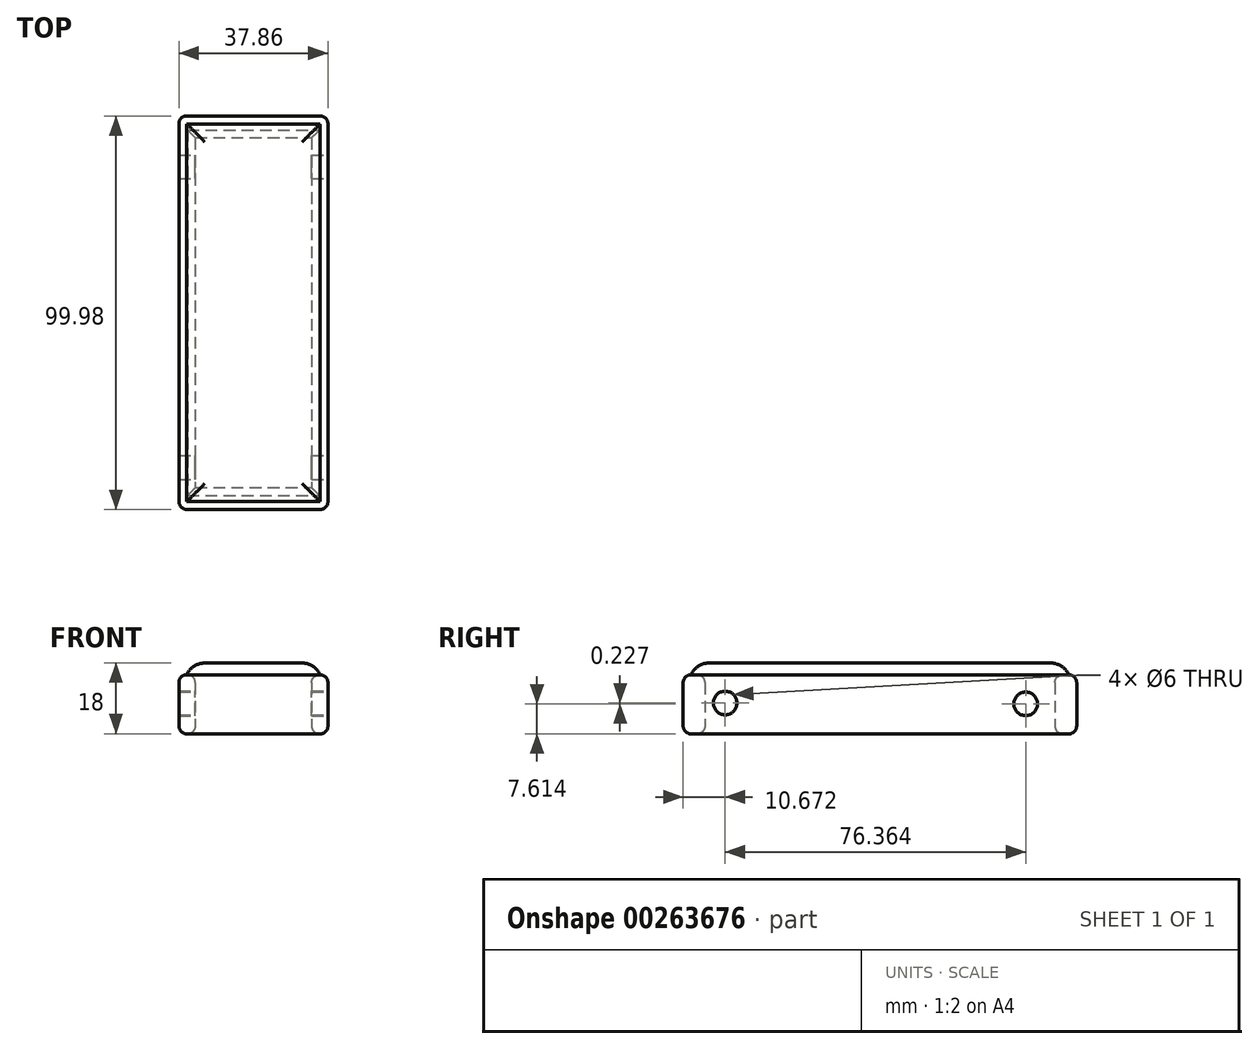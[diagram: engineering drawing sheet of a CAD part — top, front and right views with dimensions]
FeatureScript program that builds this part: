
annotation { "Feature Type Name" : "Feature", "Feature Type Description" : "" }
export const myFeature = defineFeature(function(context is Context, id is Id, definition is map)
    precondition{}
    {
        {
            var Q0;
            Q0=qCreatedBy(makeId("Top.planeOp"),FACE);
            var sketch = newSketch(context, id + "F0", { "sketchPlane" : qUnion([Q0])});
            skLineSegment(sketch, "E0.bottom", {"start": v(-18.93, 50) * mm, "end": v(18.93, 50) * mm});
            skLineSegment(sketch, "E0.top", {"start": v(-18.93, -50) * mm, "end": v(18.93, -50) * mm});
            skLineSegment(sketch, "E0.left", {"start": v(-18.93, 50) * mm, "end": v(-18.93, -50) * mm});
            skLineSegment(sketch, "E0.right", {"start": v(18.93, 50) * mm, "end": v(18.93, -50) * mm});
            skPoint(sketch, "E0.middle", {"position": v(0, 0) * mm});
            skLineSegment(sketch, "E1.bottom", {"start": v(-14.78, 44.45) * mm, "end": v(14.78, 44.45) * mm});
            skLineSegment(sketch, "E1.top", {"start": v(-14.78, -44.45) * mm, "end": v(14.78, -44.45) * mm});
            skLineSegment(sketch, "E1.left", {"start": v(-14.78, 44.45) * mm, "end": v(-14.78, -44.45) * mm});
            skLineSegment(sketch, "E1.right", {"start": v(14.78, 44.45) * mm, "end": v(14.78, -44.45) * mm});
            skSolve(sketch);
        }
        {
            var Q0;
            Q0 = qSketchRegion(id + "F0", true);
            extrude(context, id + "F1", {"entities" : qUnion([Q0]), "depth" : 15 * mm});
        }
        {
            var Q0;
            Q0=makeQuery(id+"F1.opExtrude","CAP_EDGE",EDGE,{"disambiguationData":[OSD([sQuery(id+"F0.wireOp",EDGE,"E0.bottom")])],"isStart":false});
            var Q1;
            Q1=makeQuery(id+"F1.opExtrude","CAP_EDGE",EDGE,{"disambiguationData":[OSD([sQuery(id+"F0.wireOp",EDGE,"E0.left")])],"isStart":false});
            var Q2;
            Q2=makeQuery(id+"F1.opExtrude","CAP_EDGE",EDGE,{"disambiguationData":[OSD([sQuery(id+"F0.wireOp",EDGE,"E0.top")])],"isStart":false});
            var Q3;
            Q3=makeQuery(id+"F1.opExtrude","CAP_EDGE",EDGE,{"disambiguationData":[OSD([sQuery(id+"F0.wireOp",EDGE,"E0.right")])],"isStart":false});
            var Q4;
            Q4=makeQuery(id+"F1.opExtrude","SWEPT_EDGE",EDGE,{"disambiguationData":[OSD([sQuery(id+"F0.wireOp",EDGE,"E0.bottom"),sQuery(id+"F0.wireOp",EDGE,"E0.left")])]});
            var Q5;
            Q5=makeQuery(id+"F1.opExtrude","SWEPT_EDGE",EDGE,{"disambiguationData":[OSD([sQuery(id+"F0.wireOp",EDGE,"E0.top"),sQuery(id+"F0.wireOp",EDGE,"E0.left")])]});
            var Q6;
            Q6=makeQuery(id+"F1.opExtrude","SWEPT_EDGE",EDGE,{"disambiguationData":[OSD([sQuery(id+"F0.wireOp",EDGE,"E0.bottom"),sQuery(id+"F0.wireOp",EDGE,"E0.right")])]});
            var Q7;
            Q7=makeQuery(id+"F1.opExtrude","SWEPT_EDGE",EDGE,{"disambiguationData":[OSD([sQuery(id+"F0.wireOp",EDGE,"E0.top"),sQuery(id+"F0.wireOp",EDGE,"E0.right")])]});
            var Q8;
            Q8=makeQuery(id+"F1.opExtrude","CAP_EDGE",EDGE,{"disambiguationData":[OSD([sQuery(id+"F0.wireOp",EDGE,"E1.right")])],"isStart":false});
            var Q9;
            Q9=makeQuery(id+"F1.opExtrude","CAP_EDGE",EDGE,{"disambiguationData":[OSD([sQuery(id+"F0.wireOp",EDGE,"E1.left")])],"isStart":false});
            var Q10;
            Q10=makeQuery(id+"F1.opExtrude","CAP_EDGE",EDGE,{"disambiguationData":[OSD([sQuery(id+"F0.wireOp",EDGE,"E1.top")])],"isStart":false});
            var Q11;
            Q11=makeQuery(id+"F1.opExtrude","CAP_EDGE",EDGE,{"disambiguationData":[OSD([sQuery(id+"F0.wireOp",EDGE,"E1.bottom")])],"isStart":false});
            var Q12;
            Q12=makeQuery(id+"F1.opExtrude","CAP_EDGE",EDGE,{"disambiguationData":[OSD([sQuery(id+"F0.wireOp",EDGE,"E1.top")])],"isStart":true});
            var Q13;
            Q13=makeQuery(id+"F1.opExtrude","CAP_EDGE",EDGE,{"disambiguationData":[OSD([sQuery(id+"F0.wireOp",EDGE,"E0.top")])],"isStart":true});
            var Q14;
            Q14=makeQuery(id+"F1.opExtrude","CAP_EDGE",EDGE,{"disambiguationData":[OSD([sQuery(id+"F0.wireOp",EDGE,"E1.left")])],"isStart":true});
            var Q15;
            Q15=makeQuery(id+"F1.opExtrude","CAP_EDGE",EDGE,{"disambiguationData":[OSD([sQuery(id+"F0.wireOp",EDGE,"E0.right")])],"isStart":true});
            var Q16;
            Q16=makeQuery(id+"F1.opExtrude","CAP_EDGE",EDGE,{"disambiguationData":[OSD([sQuery(id+"F0.wireOp",EDGE,"E1.right")])],"isStart":true});
            var Q17;
            Q17=makeQuery(id+"F1.opExtrude","CAP_EDGE",EDGE,{"disambiguationData":[OSD([sQuery(id+"F0.wireOp",EDGE,"E1.bottom")])],"isStart":true});
            var Q18;
            Q18=makeQuery(id+"F1.opExtrude","CAP_EDGE",EDGE,{"disambiguationData":[OSD([sQuery(id+"F0.wireOp",EDGE,"E0.bottom")])],"isStart":true});
            var Q19;
            Q19=makeQuery(id+"F1.opExtrude","CAP_EDGE",EDGE,{"disambiguationData":[OSD([sQuery(id+"F0.wireOp",EDGE,"E0.left")])],"isStart":true});
            fillet(context, id + "F2", {"entities" : qUnion([Q0, Q1, Q2, Q3, Q4, Q5, Q6, Q7, Q8, Q9, Q10, Q11, Q12, Q13, Q14, Q15, Q16, Q17, Q18, Q19]), "radius" : 2 * mm, "tangentPropagation" : true, "allowEdgeOverflow" : false});
        }
        {
            var Q0;
            Q0=makeQuery(id+"F1.opExtrude","CAP_FACE",FACE,{"disambiguationData":[OSD([sQuery(id+"F0.wireOp",EDGE,"E0.bottom"),sQuery(id+"F0.wireOp",EDGE,"E0.top"),sQuery(id+"F0.wireOp",EDGE,"E0.left"),sQuery(id+"F0.wireOp",EDGE,"E0.right"),sQuery(id+"F0.wireOp",EDGE,"E1.bottom"),sQuery(id+"F0.wireOp",EDGE,"E1.top"),sQuery(id+"F0.wireOp",EDGE,"E1.left"),sQuery(id+"F0.wireOp",EDGE,"E1.right")])],"isStart":false});
            var sketch = newSketch(context, id + "F3", { "sketchPlane" : qUnion([Q0])});
            skLineSegment(sketch, "E2.bottom", {"start": v(-16.93, 48) * mm, "end": v(16.93, 48) * mm});
            skLineSegment(sketch, "E2.top", {"start": v(-16.93, -48) * mm, "end": v(16.93, -48) * mm});
            skLineSegment(sketch, "E2.left", {"start": v(-16.93, 48) * mm, "end": v(-16.93, -48) * mm});
            skLineSegment(sketch, "E2.right", {"start": v(16.93, 48) * mm, "end": v(16.93, -48) * mm});
            skSolve(sketch);
        }
        {
            var Q0;
            Q0 = qSketchRegion(id + "F3", true);
            extrude(context, id + "F4", {"entities" : qUnion([Q0]), "operationType" : NewBodyOperationType.ADD, "depth" : 3 * mm});
        }
        {
            var Q0;
            Q0=makeQuery(id+"F1.opExtrude","SWEPT_FACE",FACE,{"disambiguationData":[OSD([sQuery(id+"F0.wireOp",EDGE,"E0.right")])]});
            var sketch = newSketch(context, id + "F5", { "sketchPlane" : qUnion([Q0])});
            skCircle(sketch, "E3", {"center": v(-39.32, 7.84) * mm, "radius": 3.23 * mm});
            skCircle(sketch, "E4", {"center": v(37.05, 7.61) * mm, "radius": 3.23 * mm});
            skSolve(sketch);
        }
        {
            var Q0;
            Q0=sQuery(id+"F5.wireOp",VERTEX,"E3.center");
            var Q1;
            Q1=sQuery(id+"F5.wireOp",VERTEX,"E4.center");
            var Q2;
            Q2=makeQuery(id+"F1.opExtrude","SWEPT_BODY",BODY,{"disambiguationData":[OSD([sQuery(id+"F0.wireOp",EDGE,"E0.bottom"),sQuery(id+"F0.wireOp",EDGE,"E0.top"),sQuery(id+"F0.wireOp",EDGE,"E0.left"),sQuery(id+"F0.wireOp",EDGE,"E0.right"),sQuery(id+"F0.wireOp",EDGE,"E1.bottom"),sQuery(id+"F0.wireOp",EDGE,"E1.top"),sQuery(id+"F0.wireOp",EDGE,"E1.left"),sQuery(id+"F0.wireOp",EDGE,"E1.right")])]});
            hole(context, id + "F6", {"style" : HoleStyle.SIMPLE, "endStyle" : HoleEndStyle.THROUGH, "holeDiameter" : 6 * mm, "tappedDepth" : 12 * mm, "tapClearance" : 3, "locations" : qUnion([Q0, Q1]), "scope" : qUnion([Q2])});
        }
        {
            var Q0;
            Q0=makeQuery(id+"F4.opExtrude","CAP_EDGE",EDGE,{"disambiguationData":[OSD([sQuery(id+"F3.wireOp",EDGE,"E2.top")])],"isStart":false});
            var Q1;
            Q1=makeQuery(id+"F4.opExtrude","CAP_EDGE",EDGE,{"disambiguationData":[OSD([sQuery(id+"F3.wireOp",EDGE,"E2.bottom")])],"isStart":false});
            var Q2;
            Q2=makeQuery(id+"F4.opExtrude","CAP_EDGE",EDGE,{"disambiguationData":[OSD([sQuery(id+"F3.wireOp",EDGE,"E2.right")])],"isStart":false});
            var Q3;
            Q3=makeQuery(id+"F4.opExtrude","CAP_EDGE",EDGE,{"disambiguationData":[OSD([sQuery(id+"F3.wireOp",EDGE,"E2.left")])],"isStart":false});
            fillet(context, id + "F7", {"entities" : qUnion([Q0, Q1, Q2, Q3]), "radius" : 5 * mm, "tangentPropagation" : true, "allowEdgeOverflow" : false});
        }
    });
